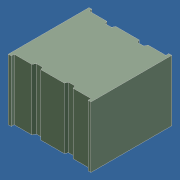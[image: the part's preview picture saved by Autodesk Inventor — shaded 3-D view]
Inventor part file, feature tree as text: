
AUTODESK INVENTOR PART (.ipt)
format: ipt  version: 2014 (Build 180170000, 170)  size: 162,816 bytes
history: native  units: in
note: dims shown in document units (in); Inventor stores cm internally (conversion verified against a paired STEP export)
features: other x21, extrude x8, sketch x8
ambient origin geometry x8: Origin, YZ Plane, XZ Plane, XY Plane, X Axis, Y Axis, Z Axis, Center Point
bodies: Solid1 (feature_tree)
feature tree (37):
  extrude  "Extrusion1"  Depth=1.0in TaperAngle=0.0deg
  extrude  "Extrusion2"  Depth=1.0in TaperAngle=0.0deg
  extrude  "Extrusion3"  Depth=1.0in TaperAngle=0.0deg
  extrude  "Extrusion4"  Depth=0.01in TaperAngle=0.0deg
  extrude  "Extrusion5"  [1 undecoded]
  extrude  "Extrusion6"  [1 undecoded]
  extrude  "Extrusion7"  [1 undecoded]
  extrude  "Extrusion8"  [1 undecoded]
  other  "rot_XY"
  other  "rot_YZ"
  other  "rot_ZX"
  other  "rot_X"
  other  "rot_Y"
  other  "rot_Z"
  other  "rot_Center"
  other  "to_cover_XY"
  other  "to_cover_YZ"
  other  "to_cover_ZX"
  other  "to_cover_X"
  other  "to_cover_Y"
  other  "to_cover_Z"
  other  "to_cover_Center"
  other  "to_terminals_XY"
  other  "to_terminals_YZ"
  other  "to_terminals_ZX"
  other  "to_terminals_X"
  other  "to_terminals_Y"
  other  "to_terminals_Z"
  other  "to_terminals_Center"
  sketch  "Sketch_2"  dims[d0=0.3877in d1=0.0in d2=1.0in d3=0.0in]
  sketch  "Sketch_8"  dims[d8=1.0in d9=0.0in d10=1.0in d11=0.0in]
  sketch  "Sketch_5"  dims[d4=1.0in d5=0.0in d6=1.0in d7=0.0in]
  sketch  "Sketch_9"  dims[d12=1.0in d13=0.0in d14=0.01in d15=0.0in]
  sketch  "Sketch_10"
  sketch  "Sketch_11"
  sketch  "Sketch_12"
  sketch  "Sketch_19"
note: 4 required parameter values undecoded (feature->parameter linkage not recoverable at this tier; creation-order binding heuristic only, values carry confidence <= 0.55)
